# Revit family: Hager-VOLTA-Flush_mounted-IP30-With_Cover-Without_DIN-Hosted-SE-en
name_source: partatom
category: Electrical Equipment
units: mm (PartAtom-declared; Revit-internal decimal feet)

## family parameters
Cut with Voids When Loaded = No
Host = Face
Maintain Annotation Orientation = Yes
Panel Configuration = Two Columns, Circuits Across
Part Type = Panelboard
Room Calculation Point = No
Round Connector Dimension = Use Diameter
Shared = No

## types (4) — shared parameters
BC_MODEL_ID = 1547277
BC_OBJECT_ID = 513508
BC_OBJECT_VERSION = #1
Code hager = ADD-EC000214_EU
EF000003 - Mounting method = Flush-mounted
EF000007 - Colour = White
EF000024 - UV resistant = No
EF000116 - RAL-number = 9010
EF000118 - With mounting plate = Yes
EF001088 - Extension possible = Yes
EF001134 - DIN-rail = No
EF004462 - Type of closure = Other
EF005474 - Degree of protection (IP) = IP30
EF006244 - Transparent cover/door = No
EF006306 - With lock = No
EF009212 - Cover model = With notch
EF015941 - Signal passing door = No
ETIM class code = EC000214
ETIM class name = Small distribution board
HG000002-With door or cover = Yes
HG000003-Range = VOLTA
HG000005-Thickness = 2 mm  [stored 0.00656168 ft]
HG000006-Flush mounted = Yes
HG000009-Double swing door = No
HG000010-Asymmetric doors = No
HG000011-Empty rows from bottom = No
HG000012-Door swing angle = 90.00°
HG000013-Door on the left = No
HG000014-Door on the right = Yes
HG000015-Clearance visibility = Yes
HG000016-Door 3D visibility = Yes
HG000017-Distance between poles = 18 mm  [stored 0.0590551 ft]
HG000060-RAL-number = 9010
HG000099-Onfly Template ID = 507532
Manufacturer = Hager
Name = VOLTA-Flush_mounted-IP30-With_Cover-Without_DIN-SE
Name BIM&CO = Electricity
Name hager = ADD_Enclosures_EC000214
Uniformat = Low Tension Service & Dist.
Uniformat code = D501001
zero-valued in all types: Default Elevation, EF001131 - Inner depth, HG000007-Number of empty columns, HG000008-Number of empty rows

## per-type parameters (varying)
| type | BC_VARIANT_ID | EF000008 - Width | EF000040 - Height | EF000049 - Depth | EF000218 - Built-in depth | EF000266 - Number of rows | EF000332 - Built-in height | EF000846 - Built-in width | EF001062 - EMC-version | EF002950 - Width in number of modular spacings | EF015776 - Earthing terminal block | EF015777 - Neutral terminal block | HG000001-Number of columns | HG000004-Manufacturer reference | HGEF000266-Number of rows | HGEF002950-Width in number of modular spacings |
| VOLTA-Flush_mounted_W426_H286_D89_18_Modular_Spacing-VU118F | 1174466 | 426 mm  [stored 1.39764 ft] | 286 mm | 89 mm  [stored 0.291995 ft] | 82 mm  [stored 0.269029 ft] | 1 | 259 mm  [stored 0.849738 ft] | 396 mm  [stored 1.29921 ft] | Yes | 18 | No | No | 1 | VU118F | 1 | 18 |
| VOLTA-Flush_mounted_W348_H630_D98_12_Modular_Spacing-VU36NW | 1174467 | 348 mm  [stored 1.14173 ft] | 630 mm  [stored 2.06693 ft] | 98 mm  [stored 0.321522 ft] | 89 mm  [stored 0.291995 ft] | 0 | 595 mm  [stored 1.9521 ft] | 315 mm | No | 12 | Yes | Yes | 0 | VU36NW | 0 | 12 |
| VOLTA-Flush_mounted_W348_H755_D98_12_Modular_Spacing-VU48NW | 1174468 | 348 mm  [stored 1.14173 ft] | 755 mm  [stored 2.47703 ft] | 98 mm  [stored 0.321522 ft] | 89 mm  [stored 0.291995 ft] | 0 | 720 mm  [stored 2.3622 ft] | 315 mm | No | 12 | No | No | 0 | VU48NW | 0 | 12 |
| VOLTA-Flush_mounted_W348_H880_D98_12_Modular_Spacing-VU60NW | 1174469 | 348 mm  [stored 1.14173 ft] | 880 mm  [stored 2.88714 ft] | 98 mm  [stored 0.321522 ft] | 89 mm  [stored 0.291995 ft] | 0 | 845 mm  [stored 2.77231 ft] | 315 mm | No | 12 | Yes | Yes | 0 | VU60NW | 0 | 12 |

note: column(s) folded — value = type name in every type: Reference

note: [stored X ft] marks values corroborated as IEEE doubles in the binary element streams (Revit-internal decimal feet)

## geometry (parser evidence)
native form markers: Sweep x14
no freeform markers — native parametric forms only
